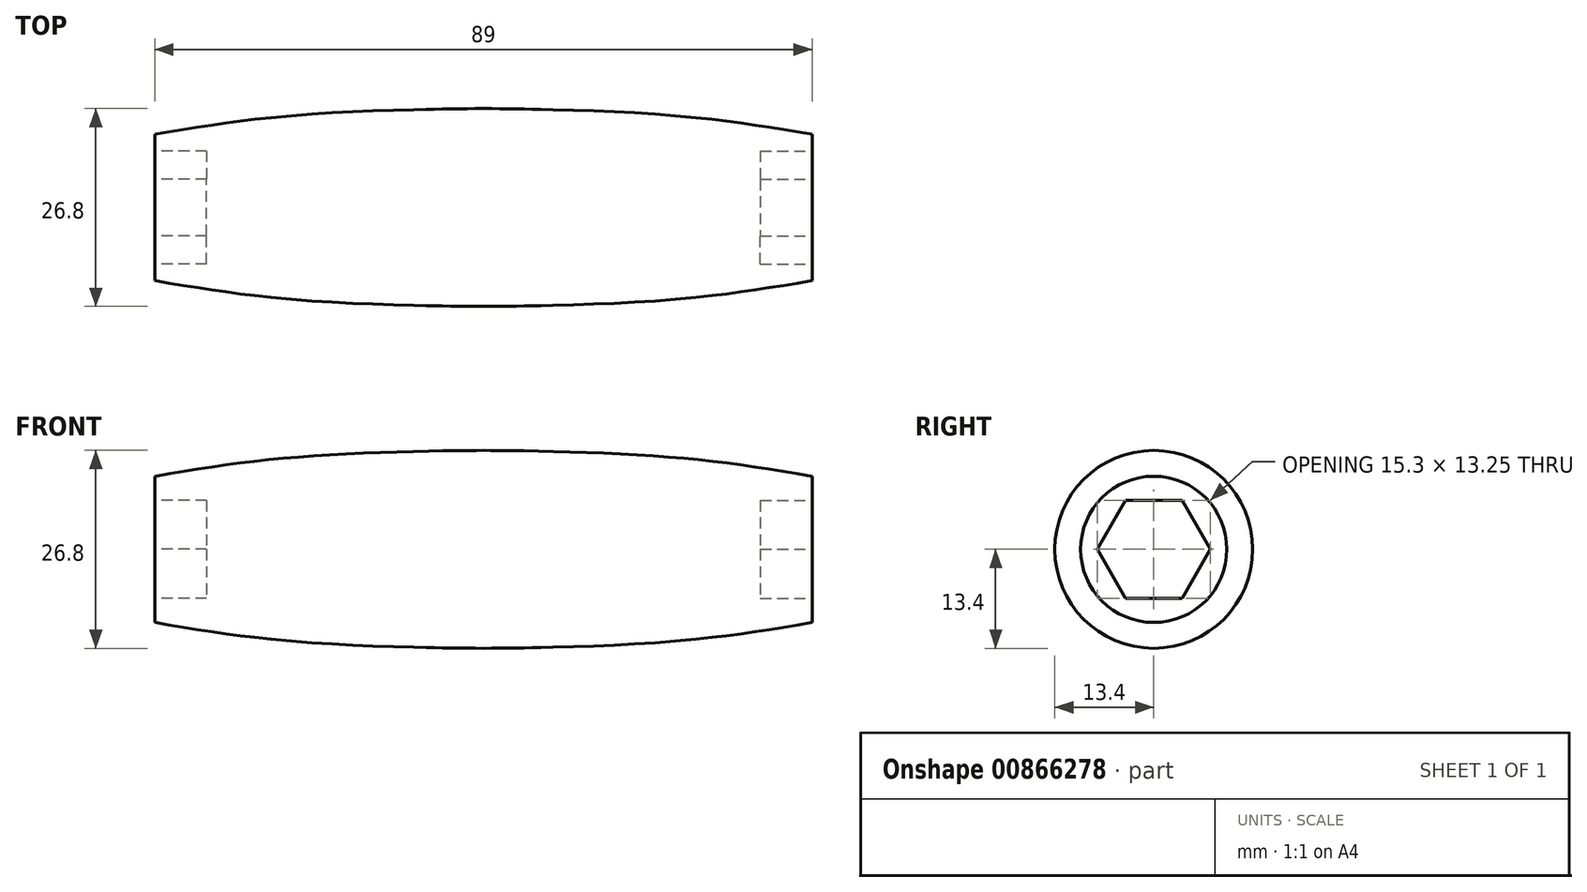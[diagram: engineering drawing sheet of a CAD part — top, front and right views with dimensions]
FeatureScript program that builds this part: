
annotation { "Feature Type Name" : "Feature", "Feature Type Description" : "" }
export const myFeature = defineFeature(function(context is Context, id is Id, definition is map)
    precondition{}
    {
        {
            var Q0;
            Q0=qCreatedBy(makeId("Front.planeOp"),FACE);
            var sketch = newSketch(context, id + "F0", { "sketchPlane" : qUnion([Q0])});
            skLineSegment(sketch, "E0", {"start": v(0, 0) * mm, "end": v(44.5, 0) * mm});
            skLineSegment(sketch, "E1", {"start": v(44.5, 0) * mm, "end": v(44.5, 9.9) * mm});
            skFitSpline(sketch, "E2", {"points": [v(0, 13.4) * mm, v(21.37, 12.77) * mm, v(44.5, 9.9) * mm], "startDerivative": vector(18.35, 0) * mm, "endDerivative": vector(46.67, -8.18) * mm});
            skLineSegment(sketch, "E3", {"start": v(44.5, 0) * mm, "end": v(0, 0) * mm});
            skLineSegment(sketch, "E4", {"start": v(0, 13.4) * mm, "end": v(0, 0) * mm});
            skFitSpline(sketch, "E5.MirrorCS", {"points": [v(0, 13.4) * mm, v(-21.37, 12.77) * mm, v(-44.5, 9.9) * mm], "startDerivative": vector(-18.35, 0) * mm, "endDerivative": vector(-46.67, -8.18) * mm});
            skLineSegment(sketch, "E6.MirrorCS", {"start": v(-44.5, 0) * mm, "end": v(-44.5, 9.9) * mm});
            skLineSegment(sketch, "E7.MirrorCS", {"start": v(-44.5, 0) * mm, "end": v(0, 0) * mm});
            skSolve(sketch);
        }
        {
            var Q0;
            Q0=makeQuery(id+"F0.imprint","IMPRINT",FACE,{"disambiguationData":[TD([[makeQuery(id+"F0.imprint","IMPRINT",EDGE,{"derivedFrom":sQuery(id+"F0.wireOp",EDGE,"E1")}),1.0]])]});
            var Q1;
            Q1=makeQuery(id+"F0.imprint","IMPRINT",FACE,{"disambiguationData":[TD([[makeQuery(id+"F0.imprint","IMPRINT",EDGE,{"derivedFrom":sQuery(id+"F0.wireOp",EDGE,"E4")}),-1.0]])]});
            var Q2;
            Q2=sQuery(id+"F0.wireOp",EDGE,"E0");
            revolve(context, id + "F1", {"surfaceOperationType" : NewSurfaceOperationType.NEW, "entities" : qUnion([Q0, Q1]), "axis" : qUnion([Q2]), "revolveType" : RevolveType.FULL});
        }
        {
            var Q0;
            Q0=makeQuery(id+"F1.opRevolve","SWEPT_FACE",FACE,{"disambiguationData":[OSD([sQuery(id+"F0.wireOp",EDGE,"E1")])]});
            var sketch = newSketch(context, id + "F2", { "sketchPlane" : qUnion([Q0])});
            skCircle(sketch, "E8.cCircle", {"center": v(0, 0) * mm, "radius": 6.62 * mm, "construction": true});
            skLineSegment(sketch, "E8.0", {"start": v(3.82, -6.62) * mm, "end": v(-3.82, -6.62) * mm});
            skLineSegment(sketch, "E8.1", {"start": v(-3.82, -6.63) * mm, "end": v(-7.65, 0) * mm});
            skLineSegment(sketch, "E8.2", {"start": v(-7.65, 0) * mm, "end": v(-3.82, 6.62) * mm});
            skLineSegment(sketch, "E8.3", {"start": v(-3.82, 6.62) * mm, "end": v(3.82, 6.63) * mm});
            skLineSegment(sketch, "E8.4", {"start": v(3.82, 6.63) * mm, "end": v(7.65, 0) * mm});
            skLineSegment(sketch, "E8.5", {"start": v(7.65, 0) * mm, "end": v(3.82, -6.63) * mm});
            skPoint(sketch, "E8.0.midPoint", {"position": v(0, -6.62) * mm});
            skSolve(sketch);
        }
        {
            var Q0;
            Q0=qSketchRegion(id+"F2",true);
            extrude(context, id + "F3", {"entities" : qUnion([Q0]), "operationType" : NewBodyOperationType.REMOVE, "oppositeDirection" : true, "depth" : 7 * mm, "offsetDistance" : 25 * mm});
        }
        {
            var Q0;
            Q0=makeQuery(id+"F1.opRevolve","SWEPT_FACE",FACE,{"disambiguationData":[OSD([sQuery(id+"F0.wireOp",EDGE,"E6.MirrorCS")])]});
            var sketch = newSketch(context, id + "F4", { "sketchPlane" : qUnion([Q0])});
            skCircle(sketch, "E9.cCircle", {"center": v(0, 0) * mm, "radius": 6.62 * mm, "construction": true});
            skLineSegment(sketch, "E9.0", {"start": v(3.82, -6.62) * mm, "end": v(-3.82, -6.62) * mm});
            skLineSegment(sketch, "E9.1", {"start": v(-3.82, -6.62) * mm, "end": v(-7.65, 0) * mm});
            skLineSegment(sketch, "E9.2", {"start": v(-7.65, 0) * mm, "end": v(-3.82, 6.62) * mm});
            skLineSegment(sketch, "E9.3", {"start": v(-3.82, 6.62) * mm, "end": v(3.82, 6.63) * mm});
            skLineSegment(sketch, "E9.4", {"start": v(3.82, 6.63) * mm, "end": v(7.65, 0) * mm});
            skLineSegment(sketch, "E9.5", {"start": v(7.65, 0) * mm, "end": v(3.82, -6.63) * mm});
            skPoint(sketch, "E9.0.midPoint", {"position": v(0, -6.62) * mm});
            skSolve(sketch);
        }
        {
            var Q0;
            Q0=qSketchRegion(id+"F4",true);
            extrude(context, id + "F5", {"entities" : qUnion([Q0]), "operationType" : NewBodyOperationType.REMOVE, "oppositeDirection" : true, "depth" : 7 * mm, "offsetDistance" : 25 * mm});
        }
    });
